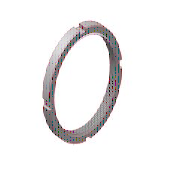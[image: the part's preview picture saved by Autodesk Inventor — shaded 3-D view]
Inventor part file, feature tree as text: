
AUTODESK INVENTOR PART (.ipt)
format: ipt  version: 2021 (Build 250183000, 183)  size: 206,848 bytes
history: native  units: mm (DEFAULTED — no unit token found)
features: sketch x3, hole x1, extrude x1, pattern_circular x1, other x1, plane x1
ambient origin geometry x8: Origin, YZ Plane, XZ Plane, XY Plane, X Axis, Y Axis, Z Axis, Center Point
bodies: Solid1 (feature_tree), Body (feature_tree)
feature tree (8):
  hole  "Thread"  [1 undecoded]
  extrude  "Groove1"  Depth=2.1mm
  pattern_circular  "Grooves1"  Angle=30.0deg  [1 undecoded]
  other  "Work Axis1"
  plane  "Work Plane1"
  sketch  "Sketch1"  dims[d0=90.0deg d1=160.0mm]
  sketch  "Sketch2"  dims[d2=21.0mm]
  sketch  "Sketch3"  dims[d3=122.834936mm d4=6.0mm d5=4.0mm d6=2.0mm d7=14.3117mm d8=8.0mm d9=0.0mm d10=6.0mm d11=30.0deg d12=6.0mm d13=6.0mm d14=75.0mm d23=10.0mm d15=0.0mm d16=40.0mm d17=360.0deg d18=2.1mm d19=3.125mm d20=45.0deg d21=3.125mm d22=45.0deg d25=0.0mm d40=6.0mm d41=3.125mm d42=3.125mm d45=90.0deg d47=0.0mm d48=0.0mm]
note: 2 required parameter values undecoded (feature->parameter linkage not recoverable at this tier; creation-order binding heuristic only, values carry confidence <= 0.55)
